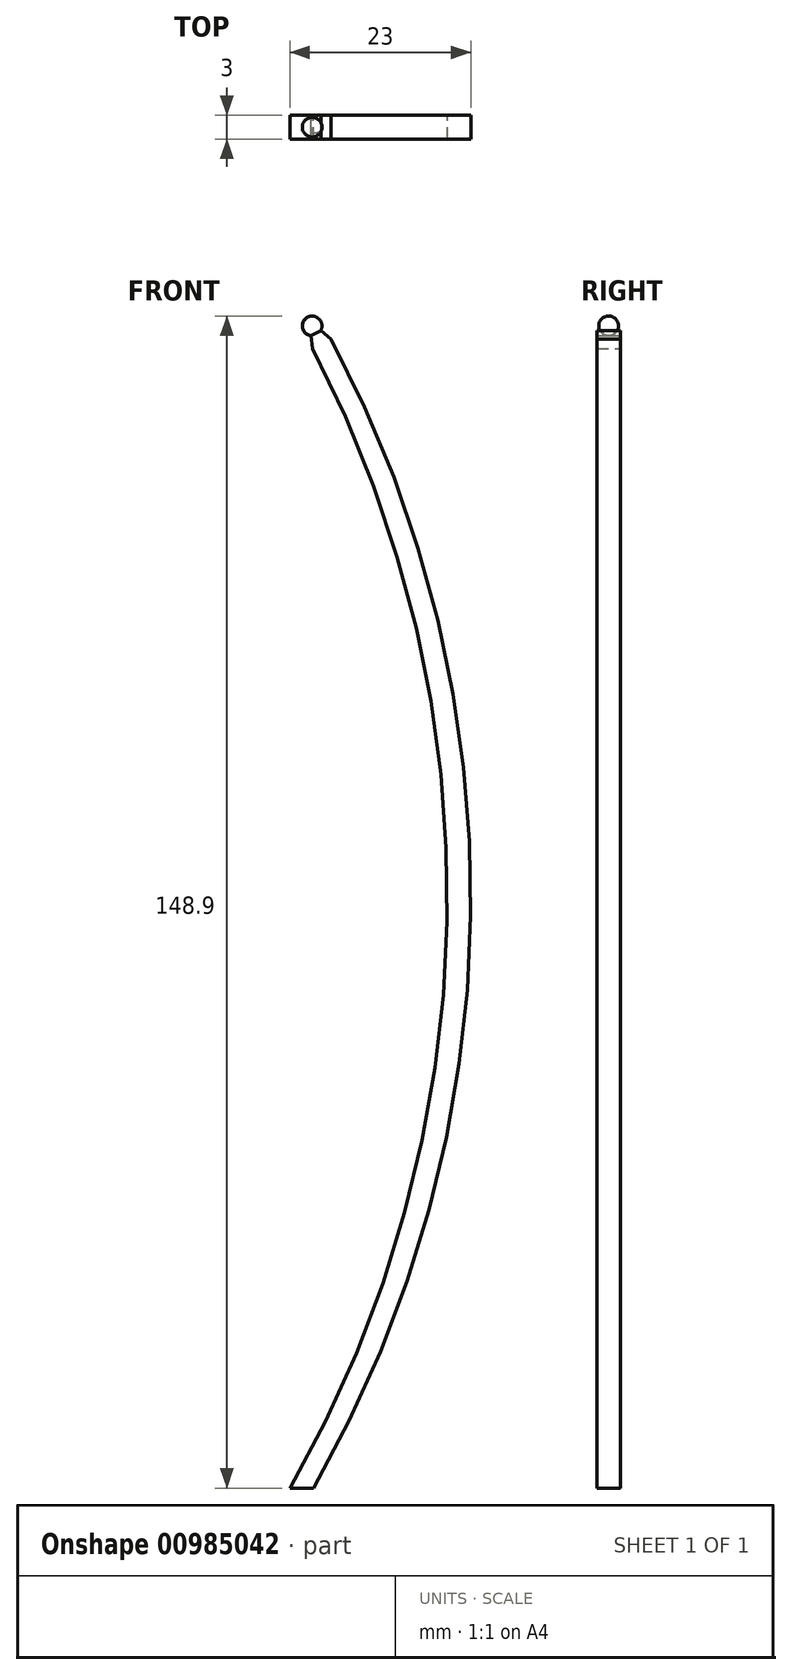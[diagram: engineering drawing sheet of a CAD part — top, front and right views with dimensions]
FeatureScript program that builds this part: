
annotation { "Feature Type Name" : "Feature", "Feature Type Description" : "" }
export const myFeature = defineFeature(function(context is Context, id is Id, definition is map)
    precondition{}
    {
        {
            var Q0;
            Q0=qCreatedBy(makeId("Front.planeOp"),FACE);
            var sketch = newSketch(context, id + "F0", { "sketchPlane" : qUnion([Q0])});
            skArc(sketch, "E0", {"start": v(0, -75) * mm, "mid": v(19.97, -3) * mm, "end": v(2.87, 69.75) * mm});
            skArc(sketch, "E1", {"start": v(3, -75) * mm, "mid": v(22.98, -2.29) * mm, "end": v(5.22, 71) * mm});
            skLineSegment(sketch, "E2", {"start": v(0, -75) * mm, "end": v(3, -75) * mm});
            skLineSegment(sketch, "E3", {"start": v(3.97, 72.07) * mm, "end": v(3.96, 72.08) * mm});
            skLineSegment(sketch, "E4", {"start": v(2.69, 71.4) * mm, "end": v(3.96, 72.08) * mm});
            skLineSegment(sketch, "E5", {"start": v(2.87, 69.75) * mm, "end": v(2.69, 71.4) * mm});
            skLineSegment(sketch, "E6.MirrorCS", {"start": v(5.22, 71) * mm, "end": v(3.96, 72.08) * mm});
            skSolve(sketch);
        }
        {
            var Q0;
            Q0=makeQuery(id+"F0.imprint","IMPRINT",FACE,{"disambiguationData":[TD([[makeQuery(id+"F0.imprint","IMPRINT",EDGE,{"derivedFrom":sQuery(id+"F0.wireOp",EDGE,"E0")}),-1.0]])]});
            extrude(context, id + "F1", {"entities" : qUnion([Q0]), "surfaceOperationType" : NewSurfaceOperationType.ADD, "endBound" : BoundingType.SYMMETRIC, "depth" : 3 * mm, "offsetDistance" : 25 * mm});
        }
        {
            var Q0;
            Q0=qCreatedBy(makeId("Front.planeOp"),FACE);
            var sketch = newSketch(context, id + "F2", { "sketchPlane" : qUnion([Q0])});
            skArc(sketch, "E7", {"start": v(2.26, 73.75) * mm, "mid": v(1.74, 72.06) * mm, "end": v(3.43, 71.54) * mm});
            skLineSegment(sketch, "E8", {"start": v(2.72, 72.88) * mm, "end": v(2.03, 74.18) * mm, "construction": true});
            skLineSegment(sketch, "E9", {"start": v(2.26, 73.75) * mm, "end": v(3.43, 71.54) * mm});
            skSolve(sketch);
        }
        {
            var Q0;
            Q0=qCreatedBy(makeId("Front.planeOp"),FACE);
            var sketch = newSketch(context, id + "F3", { "sketchPlane" : qUnion([Q0])});
            skArc(sketch, "E10", {"start": v(2.24, 73.8) * mm, "mid": v(1.55, 72.76) * mm, "end": v(2.04, 71.62) * mm});
            skArc(sketch, "E11", {"start": v(1.77, 74.68) * mm, "mid": v(0.55, 72.72) * mm, "end": v(1.64, 70.69) * mm});
            skLineSegment(sketch, "E12", {"start": v(1.64, 70.69) * mm, "end": v(2.04, 71.62) * mm});
            skLineSegment(sketch, "E13", {"start": v(3.94, 70.57) * mm, "end": v(1.12, 75.9) * mm, "construction": true});
            skLineSegment(sketch, "E14", {"start": v(1.77, 74.68) * mm, "end": v(2.24, 73.8) * mm});
            skSolve(sketch);
        }
        {
            var Q0;
            Q0=makeQuery(id+"F3.imprint","IMPRINT",FACE,{"disambiguationData":[TD([[makeQuery(id+"F3.imprint","IMPRINT",EDGE,{"derivedFrom":sQuery(id+"F3.wireOp",EDGE,"E10")}),-1.0]])]});
            var Q1;
            Q1=sQuery(id+"F3.wireOp",EDGE,"E13");
            revolve(context, id + "F4", {"surfaceOperationType" : NewSurfaceOperationType.NEW, "entities" : qUnion([Q0]), "axis" : qUnion([Q1]), "revolveType" : RevolveType.FULL});
        }
        {
            var Q0;
            Q0=qCreatedBy(makeId("Front.planeOp"),FACE);
            var sketch = newSketch(context, id + "F5", { "sketchPlane" : qUnion([Q0])});
            skLineSegment(sketch, "E15", {"start": v(-11.56, 66.73) * mm, "end": v(-4.22, 70.6) * mm});
            skLineSegment(sketch, "E16", {"start": v(15.84, 81.22) * mm, "end": v(13.04, 86.53) * mm});
            skLineSegment(sketch, "E17", {"start": v(13.04, 86.53) * mm, "end": v(-14.36, 72.03) * mm});
            skLineSegment(sketch, "E18", {"start": v(-14.36, 72.03) * mm, "end": v(-11.56, 66.73) * mm});
            skLineSegment(sketch, "E19", {"start": v(-11.66, 71.2) * mm, "end": v(-10.73, 69.43) * mm});
            skLineSegment(sketch, "E20", {"start": v(-10.73, 69.43) * mm, "end": v(13.14, 82.06) * mm});
            skLineSegment(sketch, "E21", {"start": v(13.14, 82.06) * mm, "end": v(12.2, 83.82) * mm});
            skLineSegment(sketch, "E22", {"start": v(12.2, 83.82) * mm, "end": v(-11.66, 71.2) * mm});
            skLineSegment(sketch, "E23", {"start": v(-4.22, 70.6) * mm, "end": v(1.15, 71.17) * mm});
            skLineSegment(sketch, "E24.MirrorCS", {"start": v(8.5, 77.34) * mm, "end": v(5.02, 73.22) * mm});
            skArc(sketch, "E25", {"start": v(5.02, 73.22) * mm, "mid": v(1.8, 74.64) * mm, "end": v(1.15, 71.17) * mm});
            skLineSegment(sketch, "E26.trimOffspring", {"start": v(8.5, 77.34) * mm, "end": v(15.84, 81.22) * mm});
            skSolve(sketch);
        }
        {
            var Q0;
            Q0 = qSketchRegion(id + "F5", true);
            extrude(context, id + "F6", {"entities" : qUnion([Q0]), "operationType" : NewBodyOperationType.ADD, "oppositeDirection" : true, "depth" : 2 * mm, "offsetDistance" : 25 * mm, "hasSecondDirection" : true, "secondDirectionOppositeDirection" : false, "secondDirectionDepth" : 3 * mm});
        }
        {
            var Q0;
            Q0=qCreatedBy(makeId("Front.planeOp"),FACE);
            cPlane(context, id + "F7", {"entities" : qUnion([Q0]), "cplaneType" : CPlaneType.OFFSET, "offset" : 1.5 * mm, "oppositeDirection" : true, "width" : 150 * mm, "height" : 150 * mm});
        }
        {
            var Q0;
            Q0=qCreatedBy(id+"F7.planeOp",FACE);
            var sketch = newSketch(context, id + "F8", { "sketchPlane" : qUnion([Q0])});
            skLineSegment(sketch, "E27.bottom", {"start": v(17.12, 90.68) * mm, "end": v(-16.78, 90.68) * mm});
            skLineSegment(sketch, "E27.top", {"start": v(17.12, 64.46) * mm, "end": v(-16.78, 64.46) * mm});
            skLineSegment(sketch, "E27.left", {"start": v(17.12, 90.68) * mm, "end": v(17.12, 64.46) * mm});
            skLineSegment(sketch, "E27.right", {"start": v(-16.78, 90.68) * mm, "end": v(-16.78, 64.46) * mm});
            skSolve(sketch);
        }
        {
            var Q0;
            Q0 = qSketchRegion(id + "F8", true);
            extrude(context, id + "F9", {"entities" : qUnion([Q0]), "operationType" : NewBodyOperationType.REMOVE, "oppositeDirection" : true, "depth" : 4 * mm, "offsetDistance" : 25 * mm});
        }
        {
            var Q0;
            Q0=makeQuery(id+"F6.opExtrude","CAP_EDGE",EDGE,{"disambiguationData":[OSD([sQuery(id+"F5.wireOp",EDGE,"E25")])],"isStart":true});
            var Q1;
            Q1=makeQuery(id+"F6.opExtrude","CAP_EDGE",EDGE,{"disambiguationData":[OSD([sQuery(id+"F5.wireOp",EDGE,"E25")])],"isStart":false});
            chamfer(context, id + "F10", {"entities" : qUnion([Q0, Q1]), "width" : 2 * mm, "tangentPropagation" : true});
        }
        {
            var Q0;
            Q0=makeQuery(id+"F2.imprint","IMPRINT",FACE,{"disambiguationData":[TD([[makeQuery(id+"F2.imprint","IMPRINT",EDGE,{"derivedFrom":sQuery(id+"F2.wireOp",EDGE,"E7")}),1.0]])]});
            var Q1;
            Q1=sQuery(id+"F2.wireOp",EDGE,"E8");
            revolve(context, id + "F11", {"operationType" : NewBodyOperationType.ADD, "surfaceOperationType" : NewSurfaceOperationType.NEW, "entities" : qUnion([Q0]), "axis" : qUnion([Q1]), "revolveType" : RevolveType.FULL});
        }
    });
